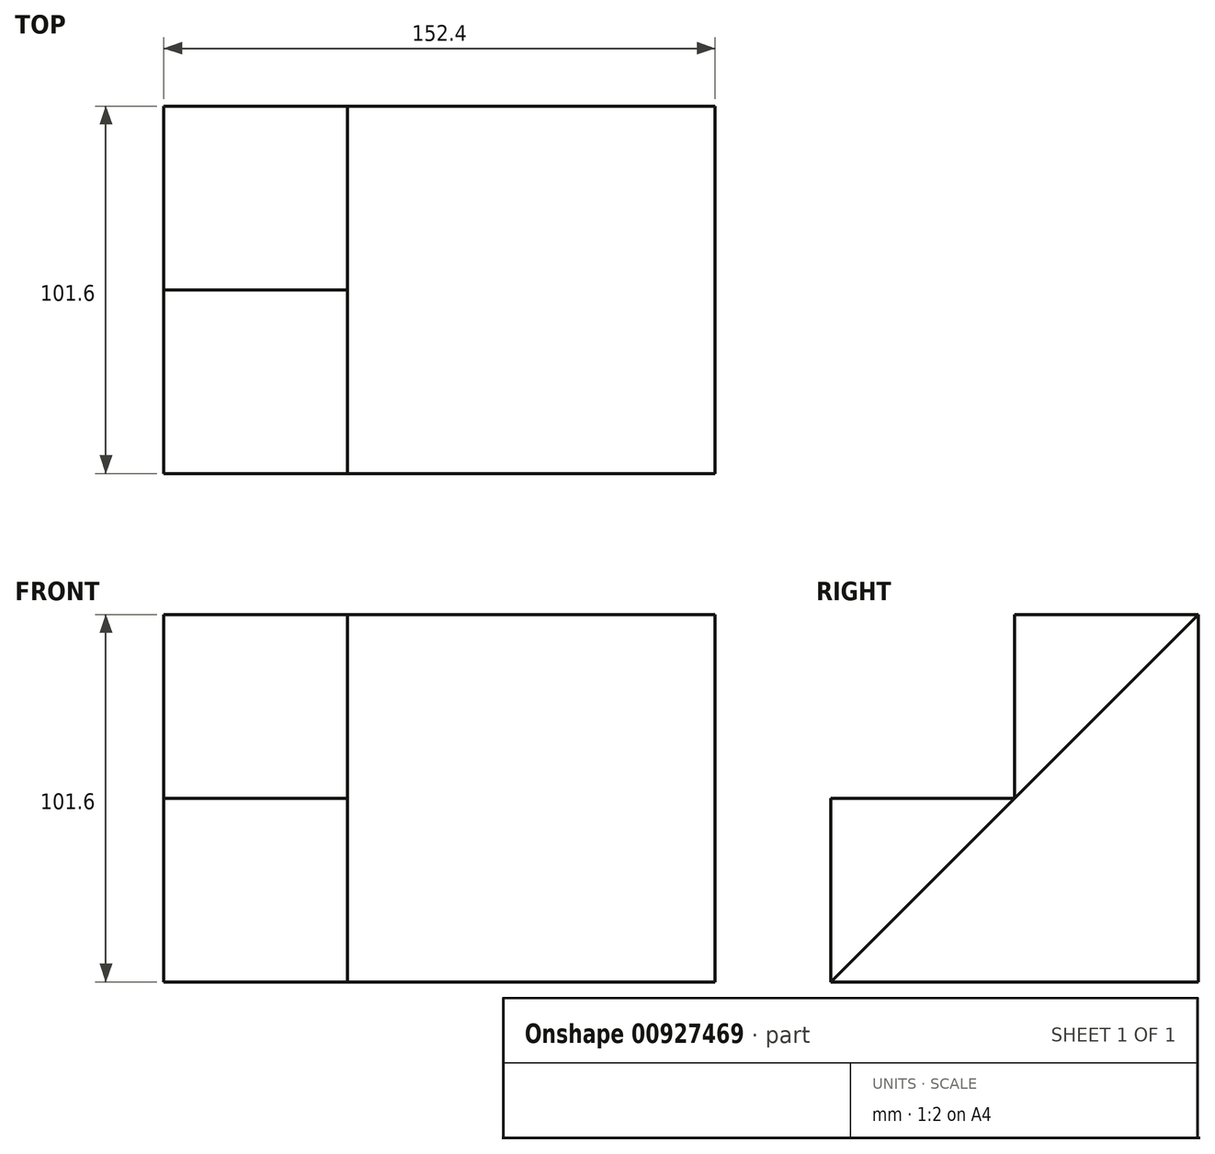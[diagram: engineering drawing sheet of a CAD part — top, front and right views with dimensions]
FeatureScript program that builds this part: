
annotation { "Feature Type Name" : "Feature", "Feature Type Description" : "" }
export const myFeature = defineFeature(function(context is Context, id is Id, definition is map)
    precondition{}
    {
        {
            var Q0;
            Q0=qCreatedBy(makeId("Right.planeOp"),FACE);
            var sketch = newSketch(context, id + "F0", { "sketchPlane" : qUnion([Q0])});
            skLineSegment(sketch, "E0", {"start": v(0, 0) * mm, "end": v(101.6, 0) * mm});
            skLineSegment(sketch, "E1", {"start": v(101.6, 0) * mm, "end": v(101.6, 101.6) * mm});
            skLineSegment(sketch, "E2", {"start": v(101.6, 101.6) * mm, "end": v(0, 0) * mm});
            skSolve(sketch);
        }
        {
            var Q0;
            Q0 = qSketchRegion(id + "F0", true);
            extrude(context, id + "F1", {"entities" : qUnion([Q0]), "depth" : 152.4 * mm, "offsetDistance" : 25.4 * mm});
        }
        {
            var Q0;
            Q0=makeQuery(id+"F1.opExtrude","CAP_FACE",FACE,{"disambiguationData":[OSD([sQuery(id+"F0.wireOp",EDGE,"E0"),sQuery(id+"F0.wireOp",EDGE,"E1"),sQuery(id+"F0.wireOp",EDGE,"E2")])],"isStart":true});
            var sketch = newSketch(context, id + "F2", { "sketchPlane" : qUnion([Q0])});
            skLineSegment(sketch, "E3", {"start": v(-101.6, 101.6) * mm, "end": v(0, 101.6) * mm});
            skLineSegment(sketch, "E4", {"start": v(0, 0) * mm, "end": v(0, 101.6) * mm});
            skSolve(sketch);
        }
        {
            var Q0;
            Q0=makeQuery(id+"F2.imprint","IMPRINT",FACE,{"disambiguationData":[TD([[makeQuery(id+"F2.imprint","IMPRINT",EDGE,{"derivedFrom":sQuery(id+"F2.wireOp",EDGE,"E3")}),-1.0]])]});
            extrude(context, id + "F3", {"entities" : qUnion([Q0]), "operationType" : NewBodyOperationType.ADD, "oppositeDirection" : true, "depth" : 50.8 * mm, "offsetDistance" : 25.4 * mm});
        }
        {
            var Q0;
            {var subQ0=sQuery(id+"F0.wireOp",EDGE,"E2");Q0=makeQuery(id+"F3.boolean.opBoolean","MERGE",FACE,{"derivedFrom":[makeQuery(id+"F1.opExtrude","CAP_FACE",FACE,{"disambiguationData":[OSD([sQuery(id+"F0.wireOp",EDGE,"E0"),sQuery(id+"F0.wireOp",EDGE,"E1"),subQ0])],"isStart":true}),makeQuery(id+"F3.opExtrude","CAP_FACE",FACE,{"disambiguationData":[OSD([subQ0,sQuery(id+"F2.wireOp",EDGE,"E3"),sQuery(id+"F2.wireOp",EDGE,"E4")])],"isStart":true})]});}
            var sketch = newSketch(context, id + "F4", { "sketchPlane" : qUnion([Q0])});
            skLineSegment(sketch, "E5.bottom", {"start": v(0, 101.6) * mm, "end": v(-50.8, 101.6) * mm});
            skLineSegment(sketch, "E5.top", {"start": v(0, 50.8) * mm, "end": v(-50.8, 50.8) * mm});
            skLineSegment(sketch, "E5.left", {"start": v(0, 101.6) * mm, "end": v(0, 50.8) * mm});
            skLineSegment(sketch, "E5.right", {"start": v(-50.8, 101.6) * mm, "end": v(-50.8, 50.8) * mm});
            skSolve(sketch);
        }
        {
            var Q0;
            Q0 = qSketchRegion(id + "F4", true);
            extrude(context, id + "F5", {"entities" : qUnion([Q0]), "operationType" : NewBodyOperationType.REMOVE, "oppositeDirection" : true, "depth" : 50.8 * mm, "offsetDistance" : 25.4 * mm});
        }
    });
